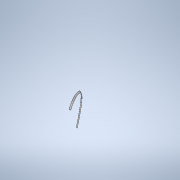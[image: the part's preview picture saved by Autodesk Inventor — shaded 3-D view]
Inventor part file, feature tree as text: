
AUTODESK INVENTOR PART (.ipt)
format: ipt  version: 2021 (Build 250183000, 183)  size: 205,312 bytes
history: native  units: in
note: dims shown in document units (in); Inventor stores cm internally (conversion verified against a paired STEP export)
features: sketch x3, sweep x1
ambient origin geometry x8: Origin, YZ Plane, XZ Plane, XY Plane, X Axis, Y Axis, Z Axis, Center Point
bodies: Solid1 (feature_tree)
feature tree (4):
  sketch  "3D Sketch1"
  sweep  "Sweep1"
  sketch  "3D Sketch2"
  sketch  "Sketch1"  dims[d6=2.0in d7=0.1in d8=2.0in d9=0.1in d10=0.0in d11=0.0in]
